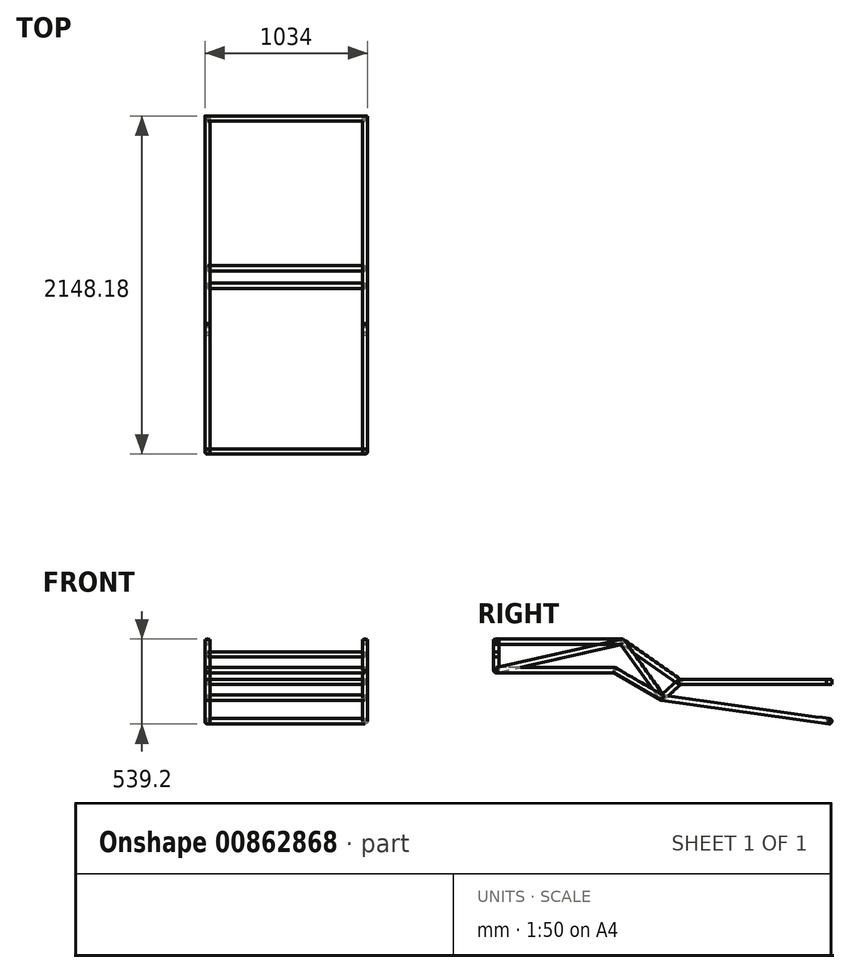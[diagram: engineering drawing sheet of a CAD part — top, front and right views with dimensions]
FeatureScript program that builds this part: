
annotation { "Feature Type Name" : "Feature", "Feature Type Description" : "" }
export const myFeature = defineFeature(function(context is Context, id is Id, definition is map)
    precondition{}
    {
        {
            var Q0;
            Q0=qCreatedBy(makeId("Top.planeOp"),FACE);
            var sketch = newSketch(context, id + "F0", { "sketchPlane" : qUnion([Q0])});
            skLineSegment(sketch, "E0", {"start": v(-500, 750) * mm, "end": v(-500, 0) * mm});
            skLineSegment(sketch, "E1", {"start": v(-500, 0) * mm, "end": v(500, 0) * mm});
            skLineSegment(sketch, "E2", {"start": v(500, 0) * mm, "end": v(500, 750) * mm});
            skLineSegment(sketch, "E3", {"start": v(0, 0) * mm, "end": v(0, 0) * mm});
            skSolve(sketch);
        }
        {
            var Q0;
            Q0=qCreatedBy(makeId("Front.planeOp"),FACE);
            var sketch = newSketch(context, id + "F1", { "sketchPlane" : qUnion([Q0])});
            skLineSegment(sketch, "E4", {"start": v(-500, 0) * mm, "end": v(-500, 180) * mm});
            skLineSegment(sketch, "E5", {"start": v(-500, 100) * mm, "end": v(500, 100) * mm});
            skLineSegment(sketch, "E6", {"start": v(500, 180) * mm, "end": v(500, 0) * mm});
            skSolve(sketch);
        }
        {
            var Q0;
            Q0=qCreatedBy(makeId("Right.planeOp"),FACE);
            cPlane(context, id + "F2", {"entities" : qUnion([Q0]), "cplaneType" : CPlaneType.OFFSET, "offset" : 500 * mm, "width" : 150 * mm, "height" : 150 * mm});
        }
        {
            var Q0;
            Q0=qCreatedBy(id+"F2.planeOp",FACE);
            var sketch = newSketch(context, id + "F3", { "sketchPlane" : qUnion([Q0])});
            skLineSegment(sketch, "E7", {"start": v(0, 180) * mm, "end": v(800, 180) * mm});
            skLineSegment(sketch, "E8", {"start": v(800, 180) * mm, "end": v(1164.18, -75) * mm});
            skLineSegment(sketch, "E9", {"start": v(750, 0) * mm, "end": v(1053.1, -175) * mm});
            skLineSegment(sketch, "E10", {"start": v(1164.18, -75) * mm, "end": v(2114.18, -75) * mm});
            skLineSegment(sketch, "E11", {"start": v(1053.1, -175) * mm, "end": v(2114.18, -325) * mm});
            skLineSegment(sketch, "E12", {"start": v(2114.18, -75) * mm, "end": v(2114.18, -325) * mm});
            skLineSegment(sketch, "E13", {"start": v(1164.18, -75) * mm, "end": v(1053.1, -175) * mm});
            skLineSegment(sketch, "E14", {"start": v(750, 0) * mm, "end": v(800, 180) * mm});
            skLineSegment(sketch, "E15", {"start": v(1053.1, -175) * mm, "end": v(800, 180) * mm});
            skLineSegment(sketch, "E16", {"start": v(800, 180) * mm, "end": v(0, 0) * mm});
            skSolve(sketch);
        }
        {
            var Q0;
            Q0=qCreatedBy(makeId("Right.planeOp"),FACE);
            cPlane(context, id + "F4", {"entities" : qUnion([Q0]), "cplaneType" : CPlaneType.OFFSET, "offset" : 500 * mm, "oppositeDirection" : true, "width" : 150 * mm, "height" : 150 * mm});
        }
        {
            var Q0;
            Q0=qCreatedBy(id+"F4.planeOp",FACE);
            var sketch = newSketch(context, id + "F5", { "sketchPlane" : qUnion([Q0])});
            skLineSegment(sketch, "E17", {"start": v(0, 180) * mm, "end": v(800, 180) * mm});
            skLineSegment(sketch, "E18", {"start": v(800, 180) * mm, "end": v(1164.18, -75) * mm});
            skLineSegment(sketch, "E19", {"start": v(1164.18, -75) * mm, "end": v(2114.18, -75) * mm});
            skLineSegment(sketch, "E20", {"start": v(2114.18, -75) * mm, "end": v(2114.18, -325) * mm});
            skLineSegment(sketch, "E21", {"start": v(2114.18, -325) * mm, "end": v(1053.1, -175) * mm});
            skLineSegment(sketch, "E22", {"start": v(1053.1, -175) * mm, "end": v(750, 0) * mm});
            skLineSegment(sketch, "E23", {"start": v(1164.18, -75) * mm, "end": v(1053.1, -175) * mm});
            skLineSegment(sketch, "E24", {"start": v(750, 0) * mm, "end": v(800, 180) * mm});
            skLineSegment(sketch, "E25", {"start": v(800, 180) * mm, "end": v(1053.1, -175) * mm});
            skLineSegment(sketch, "E26", {"start": v(800, 180) * mm, "end": v(0, 0) * mm});
            skSolve(sketch);
        }
        {
            var Q0;
            Q0=sQuery(id+"F3.wireOp",EDGE,"E12");
            var Q1;
            Q1=sQuery(id+"F5.wireOp",EDGE,"E20");
            cPlane(context, id + "F6", {"entities" : qUnion([Q0, Q1]), "cplaneType" : CPlaneType.LINE_ANGLE, "offset" : 25 * mm, "angle" : 0 * degree, "width" : 150 * mm, "height" : 150 * mm});
        }
        {
            var Q0;
            Q0=qCreatedBy(id+"F6.planeOp",FACE);
            var sketch = newSketch(context, id + "F7", { "sketchPlane" : qUnion([Q0])});
            skLineSegment(sketch, "E27", {"start": v(-500, -75) * mm, "end": v(500, -75) * mm});
            skLineSegment(sketch, "E28", {"start": v(-500, -325) * mm, "end": v(500, -325) * mm});
            skSolve(sketch);
        }
        {
            var Q0;
            Q0=sQuery(id+"F3.wireOp",EDGE,"E11");
            var Q1;
            Q1=sQuery(id+"F5.wireOp",EDGE,"E21");
            cPlane(context, id + "F8", {"entities" : qUnion([Q0, Q1]), "cplaneType" : CPlaneType.LINE_ANGLE, "offset" : 25 * mm, "angle" : 0 * degree, "width" : 150 * mm, "height" : 150 * mm});
        }
        {
            var Q0;
            Q0=qCreatedBy(id+"F8.planeOp",FACE);
            var sketch = newSketch(context, id + "F9", { "sketchPlane" : qUnion([Q0])});
            skLineSegment(sketch, "E29", {"start": v(500, 1067.24) * mm, "end": v(-500, 1067.24) * mm});
            skSolve(sketch);
        }
        {
            var Q0;
            Q0=sQuery(id+"F5.wireOp",EDGE,"E19");
            var Q1;
            Q1=sQuery(id+"F3.wireOp",EDGE,"E10");
            cPlane(context, id + "F10", {"entities" : qUnion([Q0, Q1]), "cplaneType" : CPlaneType.LINE_ANGLE, "offset" : 25 * mm, "angle" : 0 * degree, "width" : 150 * mm, "height" : 150 * mm});
        }
        {
            var Q0;
            Q0=qCreatedBy(id+"F10.planeOp",FACE);
            var sketch = newSketch(context, id + "F11", { "sketchPlane" : qUnion([Q0])});
            skLineSegment(sketch, "E30", {"start": v(500, -1164.18) * mm, "end": v(-500, -1164.18) * mm});
            skLineSegment(sketch, "E31", {"start": v(-500, -1164.18) * mm, "end": v(500, -2114.18) * mm});
            skLineSegment(sketch, "E32", {"start": v(500, -1164.18) * mm, "end": v(-500, -2114.18) * mm});
            skSolve(sketch);
        }
        {
            var Q0;
            Q0=sQuery(id+"F3.wireOp",EDGE,"E7");
            cPlane(context, id + "F12", {"entities" : qUnion([Q0]), "cplaneType" : CPlaneType.MID_PLANE, "offset" : 25 * mm, "width" : 150 * mm, "height" : 150 * mm});
        }
        {
            var Q0;
            Q0=qCreatedBy(id+"F12.planeOp",FACE);
            var sketch = newSketch(context, id + "F13", { "sketchPlane" : qUnion([Q0])});
            skCircle(sketch, "E33", {"center": v(-500, 180) * mm, "radius": 17 * mm});
            skCircle(sketch, "E34", {"center": v(500, 180) * mm, "radius": 17 * mm});
            skCircle(sketch, "E35", {"center": v(500, 0) * mm, "radius": 17 * mm});
            skCircle(sketch, "E36", {"center": v(-500, 0) * mm, "radius": 17 * mm});
            skSolve(sketch);
        }
        {
            var Q0;
            Q0=makeQuery(id+"F13.imprint","IMPRINT",FACE,{"disambiguationData":[TD([[makeQuery(id+"F13.imprint","IMPRINT",EDGE,{"derivedFrom":sQuery(id+"F13.wireOp",EDGE,"E33")}),1.0]])]});
            var Q1;
            Q1=makeQuery(id+"F13.imprint","IMPRINT",FACE,{"disambiguationData":[TD([[makeQuery(id+"F13.imprint","IMPRINT",EDGE,{"derivedFrom":sQuery(id+"F13.wireOp",EDGE,"E34")}),1.0]])]});
            extrude(context, id + "F14", {"entities" : qUnion([Q0, Q1]), "depth" : 405 * mm, "offsetDistance" : 25 * mm, "hasSecondDirection" : true, "secondDirectionOppositeDirection" : true, "secondDirectionDepth" : 405 * mm});
        }
        {
            var Q0;
            Q0=makeQuery(id+"F13.imprint","IMPRINT",FACE,{"disambiguationData":[TD([[makeQuery(id+"F13.imprint","IMPRINT",EDGE,{"derivedFrom":sQuery(id+"F13.wireOp",EDGE,"E36")}),1.0]])]});
            var Q1;
            Q1=makeQuery(id+"F13.imprint","IMPRINT",FACE,{"disambiguationData":[TD([[makeQuery(id+"F13.imprint","IMPRINT",EDGE,{"derivedFrom":sQuery(id+"F13.wireOp",EDGE,"E35")}),1.0]])]});
            extrude(context, id + "F15", {"entities" : qUnion([Q0, Q1]), "depth" : 355 * mm, "offsetDistance" : 25 * mm, "hasSecondDirection" : true, "secondDirectionOppositeDirection" : true, "secondDirectionDepth" : 405 * mm});
        }
        {
            var Q0;
            Q0=sQuery(id+"F3.wireOp",EDGE,"E8");
            cPlane(context, id + "F16", {"entities" : qUnion([Q0]), "cplaneType" : CPlaneType.MID_PLANE, "offset" : 25 * mm, "width" : 150 * mm, "height" : 150 * mm});
        }
        {
            var Q0;
            Q0=qCreatedBy(id+"F16.planeOp",FACE);
            var sketch = newSketch(context, id + "F17", { "sketchPlane" : qUnion([Q0])});
            skCircle(sketch, "E37", {"center": v(-500, 606.3) * mm, "radius": 17 * mm});
            skCircle(sketch, "E38", {"center": v(500, 606.3) * mm, "radius": 17 * mm});
            skSolve(sketch);
        }
        {
            var Q0;
            Q0=makeQuery(id+"F17.imprint","IMPRINT",FACE,{"disambiguationData":[TD([[makeQuery(id+"F17.imprint","IMPRINT",EDGE,{"derivedFrom":sQuery(id+"F17.wireOp",EDGE,"E37")}),1.0]])]});
            var Q1;
            Q1=makeQuery(id+"F17.imprint","IMPRINT",FACE,{"disambiguationData":[TD([[makeQuery(id+"F17.imprint","IMPRINT",EDGE,{"derivedFrom":sQuery(id+"F17.wireOp",EDGE,"E38")}),1.0]])]});
            extrude(context, id + "F18", {"entities" : qUnion([Q0, Q1]), "depth" : 222 * mm, "offsetDistance" : 25 * mm, "hasSecondDirection" : true, "secondDirectionOppositeDirection" : true, "secondDirectionDepth" : 228 * mm});
        }
        {
            var Q0;
            Q0=sQuery(id+"F3.wireOp",EDGE,"E9");
            cPlane(context, id + "F19", {"entities" : qUnion([Q0]), "cplaneType" : CPlaneType.MID_PLANE, "offset" : 25 * mm, "width" : 150 * mm, "height" : 150 * mm});
        }
        {
            var Q0;
            Q0=qCreatedBy(id+"F19.planeOp",FACE);
            var sketch = newSketch(context, id + "F20", { "sketchPlane" : qUnion([Q0])});
            skCircle(sketch, "E39", {"center": v(-500, 375) * mm, "radius": 17 * mm});
            skCircle(sketch, "E40", {"center": v(500, 375) * mm, "radius": 17 * mm});
            skSolve(sketch);
        }
        {
            var Q0;
            Q0 = qSketchRegion(id + "F20", true);
            extrude(context, id + "F21", {"entities" : qUnion([Q0]), "depth" : 180 * mm, "offsetDistance" : 25 * mm, "hasSecondDirection" : true, "secondDirectionOppositeDirection" : true, "secondDirectionDepth" : 180 * mm});
        }
        {
            var Q0;
            Q0=sQuery(id+"F3.wireOp",EDGE,"E10");
            cPlane(context, id + "F22", {"entities" : qUnion([Q0]), "cplaneType" : CPlaneType.MID_PLANE, "offset" : 25 * mm, "width" : 150 * mm, "height" : 150 * mm});
        }
        {
            var Q0;
            Q0=sQuery(id+"F11.wireOp",EDGE,"E30");
            cPlane(context, id + "F23", {"entities" : qUnion([Q0]), "cplaneType" : CPlaneType.MID_PLANE, "offset" : 25 * mm, "width" : 150 * mm, "height" : 150 * mm});
        }
        {
            var Q0;
            Q0=qCreatedBy(id+"F23.planeOp",FACE);
            var sketch = newSketch(context, id + "F24", { "sketchPlane" : qUnion([Q0])});
            skCircle(sketch, "E41", {"center": v(-1053.1, -175) * mm, "radius": 17 * mm});
            skCircle(sketch, "E42", {"center": v(-1164.18, -75) * mm, "radius": 17 * mm});
            skCircle(sketch, "E43", {"center": v(0, 100) * mm, "radius": 17 * mm});
            skCircle(sketch, "E44", {"center": v(0, 0) * mm, "radius": 17 * mm});
            skCircle(sketch, "E45", {"center": v(-2114.18, -75) * mm, "radius": 17 * mm});
            skCircle(sketch, "E46", {"center": v(-2114.18, -325) * mm, "radius": 17 * mm});
            skSolve(sketch);
        }
        {
            var Q0;
            Q0 = qSketchRegion(id + "F24", true);
            extrude(context, id + "F25", {"entities" : qUnion([Q0]), "depth" : 500 * mm, "offsetDistance" : 25 * mm, "hasSecondDirection" : true, "secondDirectionOppositeDirection" : true, "secondDirectionDepth" : 500 * mm});
        }
        {
            var Q0;
            Q0=sQuery(id+"F1.wireOp",EDGE,"E4");
            cPlane(context, id + "F26", {"entities" : qUnion([Q0]), "cplaneType" : CPlaneType.MID_PLANE, "offset" : 25 * mm, "width" : 150 * mm, "height" : 150 * mm});
        }
        {
            var Q0;
            Q0=qCreatedBy(id+"F26.planeOp",FACE);
            var sketch = newSketch(context, id + "F27", { "sketchPlane" : qUnion([Q0])});
            skCircle(sketch, "E47", {"center": v(-500, 0) * mm, "radius": 17 * mm});
            skCircle(sketch, "E48", {"center": v(500, 0) * mm, "radius": 17 * mm});
            skSolve(sketch);
        }
        {
            var Q0;
            Q0 = qSketchRegion(id + "F27", true);
            extrude(context, id + "F28", {"entities" : qUnion([Q0]), "depth" : 105 * mm, "offsetDistance" : 25 * mm, "hasSecondDirection" : true, "secondDirectionOppositeDirection" : true, "secondDirectionDepth" : 92 * mm});
        }
        {
            var Q0;
            Q0=sQuery(id+"F5.wireOp",EDGE,"E26");
            cPlane(context, id + "F29", {"entities" : qUnion([Q0]), "cplaneType" : CPlaneType.MID_PLANE, "offset" : 25 * mm, "width" : 150 * mm, "height" : 150 * mm});
        }
        {
            var Q0;
            Q0=qCreatedBy(id+"F29.planeOp",FACE);
            var sketch = newSketch(context, id + "F30", { "sketchPlane" : qUnion([Q0])});
            skCircle(sketch, "E49", {"center": v(-500, 0) * mm, "radius": 17 * mm});
            skCircle(sketch, "E50", {"center": v(500, 0) * mm, "radius": 17 * mm});
            skSolve(sketch);
        }
        {
            var Q0;
            Q0 = qSketchRegion(id + "F30", true);
            extrude(context, id + "F31", {"entities" : qUnion([Q0]), "depth" : 405 * mm, "offsetDistance" : 25 * mm, "hasSecondDirection" : true, "secondDirectionOppositeDirection" : true, "secondDirectionDepth" : 405 * mm});
        }
        {
            var Q0;
            Q0=sQuery(id+"F5.wireOp",EDGE,"E25");
            cPlane(context, id + "F32", {"entities" : qUnion([Q0]), "cplaneType" : CPlaneType.MID_PLANE, "offset" : 25 * mm, "width" : 150 * mm, "height" : 150 * mm});
        }
        {
            var Q0;
            Q0=qCreatedBy(id+"F32.planeOp",FACE);
            var sketch = newSketch(context, id + "F33", { "sketchPlane" : qUnion([Q0])});
            skCircle(sketch, "E51", {"center": v(-500, -755.88) * mm, "radius": 17 * mm});
            skCircle(sketch, "E52", {"center": v(500, -755.88) * mm, "radius": 17 * mm});
            skSolve(sketch);
        }
        {
            var Q0;
            Q0 = qSketchRegion(id + "F33", true);
            extrude(context, id + "F34", {"entities" : qUnion([Q0]), "depth" : 220 * mm, "offsetDistance" : 25 * mm, "hasSecondDirection" : true, "secondDirectionOppositeDirection" : true, "secondDirectionDepth" : 218 * mm});
        }
        {
            var Q0;
            Q0=sQuery(id+"F5.wireOp",EDGE,"E23");
            cPlane(context, id + "F35", {"entities" : qUnion([Q0]), "cplaneType" : CPlaneType.MID_PLANE, "offset" : 25 * mm, "width" : 150 * mm, "height" : 150 * mm});
        }
        {
            var Q0;
            Q0=qCreatedBy(id+"F35.planeOp",FACE);
            var sketch = newSketch(context, id + "F36", { "sketchPlane" : qUnion([Q0])});
            skCircle(sketch, "E53", {"center": v(-500, -834.7) * mm, "radius": 17 * mm});
            skCircle(sketch, "E54", {"center": v(500, -834.7) * mm, "radius": 17 * mm});
            skSolve(sketch);
        }
        {
            var Q0;
            Q0 = qSketchRegion(id + "F36", true);
            extrude(context, id + "F37", {"entities" : qUnion([Q0]), "depth" : 75 * mm, "offsetDistance" : 25 * mm, "hasSecondDirection" : true, "secondDirectionOppositeDirection" : true, "secondDirectionDepth" : 75 * mm});
        }
        {
            var Q0;
            Q0=qCreatedBy(id+"F22.planeOp",FACE);
            var sketch = newSketch(context, id + "F38", { "sketchPlane" : qUnion([Q0])});
            skCircle(sketch, "E55", {"center": v(-500, -75) * mm, "radius": 17 * mm});
            skCircle(sketch, "E56", {"center": v(500, -75) * mm, "radius": 17 * mm});
            skSolve(sketch);
        }
        {
            var Q0;
            Q0 = qSketchRegion(id + "F38", true);
            extrude(context, id + "F39", {"entities" : qUnion([Q0]), "depth" : 492 * mm, "offsetDistance" : 25 * mm, "hasSecondDirection" : true, "secondDirectionOppositeDirection" : true, "secondDirectionDepth" : 480 * mm});
        }
        {
            var Q0;
            Q0=sQuery(id+"F3.wireOp",EDGE,"E11");
            cPlane(context, id + "F40", {"entities" : qUnion([Q0]), "cplaneType" : CPlaneType.MID_PLANE, "offset" : 25 * mm, "width" : 150 * mm, "height" : 150 * mm});
        }
        {
            var Q0;
            Q0=qCreatedBy(id+"F40.planeOp",FACE);
            var sketch = newSketch(context, id + "F41", { "sketchPlane" : qUnion([Q0])});
            skCircle(sketch, "E57", {"center": v(-500, -25.87) * mm, "radius": 17 * mm});
            skCircle(sketch, "E58", {"center": v(500, -25.87) * mm, "radius": 17 * mm});
            skSolve(sketch);
        }
        {
            var Q0;
            Q0 = qSketchRegion(id + "F41", true);
            extrude(context, id + "F42", {"entities" : qUnion([Q0]), "depth" : 535 * mm, "offsetDistance" : 25 * mm, "hasSecondDirection" : true, "secondDirectionOppositeDirection" : true, "secondDirectionDepth" : 537 * mm});
        }
    });
